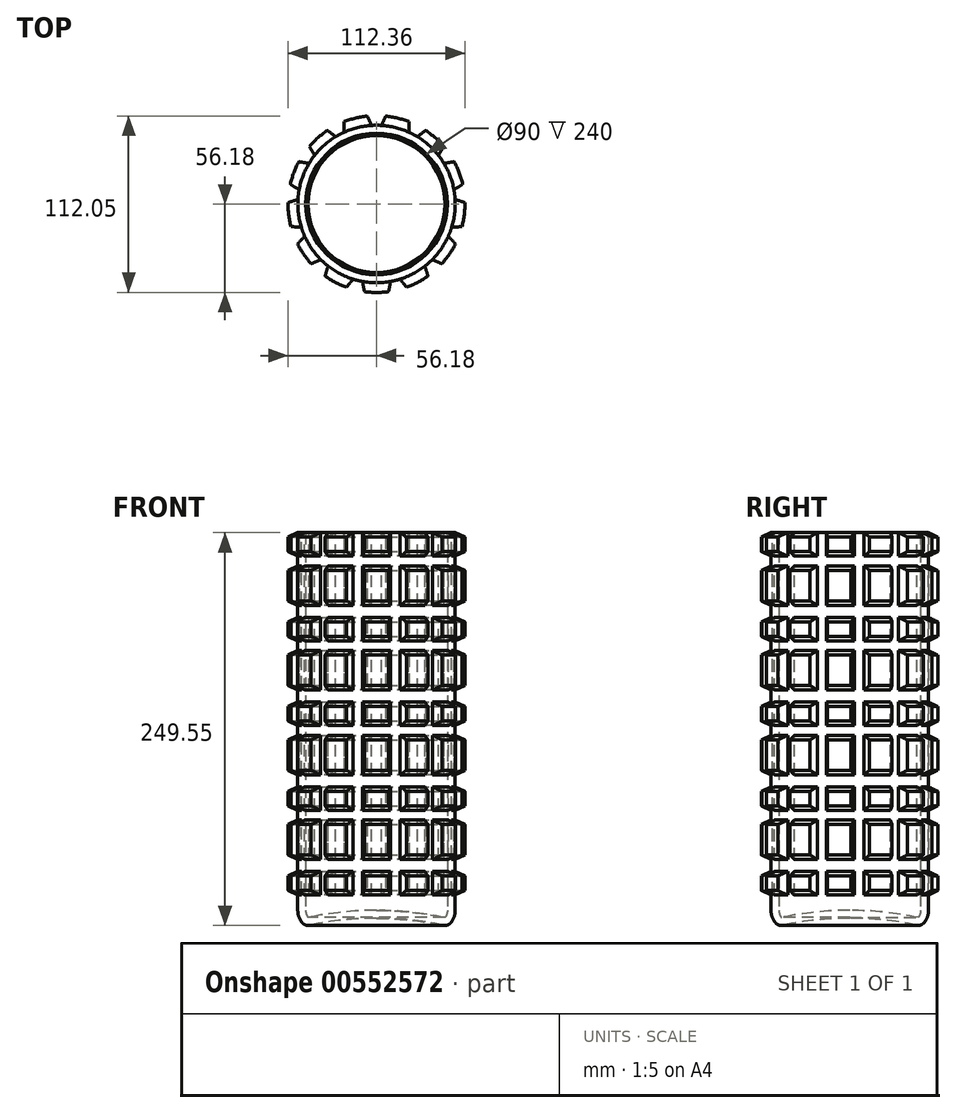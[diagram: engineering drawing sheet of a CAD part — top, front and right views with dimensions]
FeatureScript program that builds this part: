
annotation { "Feature Type Name" : "Feature", "Feature Type Description" : "" }
export const myFeature = defineFeature(function(context is Context, id is Id, definition is map)
    precondition{}
    {
        {
            var Q0;
            Q0=qCreatedBy(makeId("Front.planeOp"),FACE);
            var sketch = newSketch(context, id + "F0", { "sketchPlane" : qUnion([Q0])});
            skLineSegment(sketch, "E0", {"start": v(0, 125) * mm, "end": v(0, -125) * mm, "construction": true});
            skPoint(sketch, "E1", {"position": v(0, 0) * mm});
            skLineSegment(sketch, "E2", {"start": v(-50, 0) * mm, "end": v(50, 0) * mm, "construction": true});
            skLineSegment(sketch, "E3", {"start": v(-50, -115) * mm, "end": v(50, -115) * mm, "construction": true});
            skPoint(sketch, "E4", {"position": v(0, -115) * mm});
            skLineSegment(sketch, "E5", {"start": v(-45, -125) * mm, "end": v(45, -125) * mm, "construction": true});
            skPoint(sketch, "E6", {"position": v(0, -125) * mm});
            skLineSegment(sketch, "E7", {"start": v(0, 125) * mm, "end": v(50, 125) * mm, "construction": true});
            skLineSegment(sketch, "E8", {"start": v(50, 125) * mm, "end": v(0, 125) * mm});
            skLineSegment(sketch, "E9", {"start": v(0, -120) * mm, "end": v(45, -120) * mm, "construction": true});
            skLineSegment(sketch, "E10", {"start": v(50, -115) * mm, "end": v(50, 125) * mm, "construction": true});
            skArc(sketch, "E11", {"start": v(42.43, -124.44) * mm, "mid": v(21.33, -121.11) * mm, "end": v(0, -120) * mm});
            skArc(sketch, "E12", {"start": v(47.44, -122.58) * mm, "mid": v(49.34, -119) * mm, "end": v(50, -115) * mm});
            skPoint(sketch, "E13.visualSharp", {"position": v(45, -125) * mm});
            skArc(sketch, "E13.filletArc", {"start": v(42.43, -124.44) * mm, "mid": v(45.2, -124.23) * mm, "end": v(47.44, -122.58) * mm});
            skLineSegment(sketch, "E14", {"start": v(50, 125) * mm, "end": v(50, -115) * mm});
            skArc(sketch, "E15.0", {"start": v(43.46, -119.55) * mm, "mid": v(21.85, -116.14) * mm, "end": v(0, -115) * mm});
            skArc(sketch, "E15.1", {"start": v(43.46, -119.55) * mm, "mid": v(44.6, -117.4) * mm, "end": v(45, -115) * mm});
            skLineSegment(sketch, "E15.2", {"start": v(45, 125) * mm, "end": v(45, -115) * mm});
            skLineSegment(sketch, "E16", {"start": v(0, -120) * mm, "end": v(0, 125) * mm});
            skSolve(sketch);
        }
        {
            var Q0;
            {var subQ0=sQuery(id+"F0.wireOp",EDGE,"E11");Q0=makeQuery(id+"F0.imprint","IMPRINT",FACE,{"disambiguationData":[TD([[makeQuery(id+"F0.imprint","IMPRINT",EDGE,{"derivedFrom":subQ0}),-1.0]])]});}
            var Q1;
            Q1=sQuery(id+"F0.wireOp",EDGE,"E16");
            revolve(context, id + "F1", {"surfaceOperationType" : NewSurfaceOperationType.NEW, "entities" : qUnion([Q0]), "axis" : qUnion([Q1]), "revolveType" : RevolveType.FULL});
        }
        {
            var Q0;
            Q0=qCreatedBy(makeId("Front.planeOp"),FACE);
            var sketch = newSketch(context, id + "F2", { "sketchPlane" : qUnion([Q0])});
            skLineSegment(sketch, "E17.bottom", {"start": v(50, 125) * mm, "end": v(-50, 125) * mm, "construction": true});
            skLineSegment(sketch, "E17.top", {"start": v(50, -125) * mm, "end": v(-50, -125) * mm, "construction": true});
            skLineSegment(sketch, "E17.left", {"start": v(50, 125) * mm, "end": v(50, -125) * mm, "construction": true});
            skLineSegment(sketch, "E17.right", {"start": v(-50, 125) * mm, "end": v(-50, -125) * mm, "construction": true});
            skPoint(sketch, "E17.middle", {"position": v(0, 0) * mm});
            skLineSegment(sketch, "E18", {"start": v(50, 125) * mm, "end": v(56.18, 122.12) * mm});
            skLineSegment(sketch, "E19", {"start": v(56.18, 122.12) * mm, "end": v(56.18, 112.88) * mm});
            skLineSegment(sketch, "E20", {"start": v(56.18, 112.88) * mm, "end": v(50, 110) * mm});
            skLineSegment(sketch, "E21", {"start": v(0, 0) * mm, "end": v(0, -115) * mm, "construction": true});
            skLineSegment(sketch, "E22", {"start": v(0, -115) * mm, "end": v(50, -115) * mm, "construction": true});
            skPoint(sketch, "E23", {"position": v(50, 103.82) * mm});
            skLineSegment(sketch, "E24", {"start": v(50, 103.82) * mm, "end": v(56.18, 100.94) * mm});
            skLineSegment(sketch, "E25", {"start": v(56.18, 100.94) * mm, "end": v(56.18, 81.7) * mm});
            skLineSegment(sketch, "E26", {"start": v(56.18, 81.7) * mm, "end": v(50, 78.82) * mm});
            skLineSegment(sketch, "E27.0.1.0", {"start": v(50, 71.18) * mm, "end": v(56.18, 68.3) * mm});
            skLineSegment(sketch, "E27.0.1.1", {"start": v(56.18, 68.3) * mm, "end": v(56.18, 59.06) * mm});
            skLineSegment(sketch, "E27.0.1.2", {"start": v(56.18, 59.06) * mm, "end": v(50, 56.18) * mm});
            skLineSegment(sketch, "E27.0.1.3", {"start": v(50, 50) * mm, "end": v(56.18, 47.12) * mm});
            skLineSegment(sketch, "E27.0.1.4", {"start": v(56.18, 47.12) * mm, "end": v(56.18, 27.88) * mm});
            skLineSegment(sketch, "E27.0.1.5", {"start": v(56.18, 27.88) * mm, "end": v(50, 25) * mm});
            skLineSegment(sketch, "E27.0.2.0", {"start": v(50, 17.36) * mm, "end": v(56.18, 14.48) * mm});
            skLineSegment(sketch, "E27.0.2.1", {"start": v(56.18, 14.48) * mm, "end": v(56.18, 5.24) * mm});
            skLineSegment(sketch, "E27.0.2.2", {"start": v(56.18, 5.24) * mm, "end": v(50, 2.36) * mm});
            skLineSegment(sketch, "E27.0.2.3", {"start": v(50, -3.82) * mm, "end": v(56.18, -6.7) * mm});
            skLineSegment(sketch, "E27.0.2.4", {"start": v(56.18, -6.7) * mm, "end": v(56.18, -25.94) * mm});
            skLineSegment(sketch, "E27.0.2.5", {"start": v(56.18, -25.94) * mm, "end": v(50, -28.82) * mm});
            skLineSegment(sketch, "E27.direction1", {"start": v(50, 125) * mm, "end": v(75, 125) * mm, "construction": true});
            skLineSegment(sketch, "E27.direction2", {"start": v(50, 125) * mm, "end": v(50, 71.18) * mm, "construction": true});
            skLineSegment(sketch, "E28", {"start": v(50, -3.82) * mm, "end": v(50, -28.82) * mm});
            skLineSegment(sketch, "E29", {"start": v(50, 17.36) * mm, "end": v(50, 2.36) * mm});
            skLineSegment(sketch, "E30", {"start": v(50, 50) * mm, "end": v(50, 25) * mm});
            skLineSegment(sketch, "E31", {"start": v(50, 71.18) * mm, "end": v(50, 56.18) * mm});
            skLineSegment(sketch, "E32", {"start": v(50, 103.82) * mm, "end": v(50, 78.82) * mm});
            skLineSegment(sketch, "E33", {"start": v(50, 125) * mm, "end": v(50, 110) * mm});
            skLineSegment(sketch, "E34.0.0.3", {"start": v(50, -36.46) * mm, "end": v(56.18, -39.34) * mm});
            skLineSegment(sketch, "E34.3.0.3", {"start": v(56.18, -39.34) * mm, "end": v(56.18, -48.58) * mm});
            skLineSegment(sketch, "E34.6.0.3", {"start": v(56.18, -48.58) * mm, "end": v(50, -51.46) * mm});
            skLineSegment(sketch, "E34.9.0.3", {"start": v(50, -57.64) * mm, "end": v(56.18, -60.52) * mm});
            skLineSegment(sketch, "E34.12.0.3", {"start": v(56.18, -60.52) * mm, "end": v(56.18, -79.76) * mm});
            skLineSegment(sketch, "E34.15.0.3", {"start": v(56.18, -79.76) * mm, "end": v(50, -82.64) * mm});
            skLineSegment(sketch, "E35.0.0.4", {"start": v(50, -90.28) * mm, "end": v(56.18, -93.16) * mm});
            skLineSegment(sketch, "E35.3.0.4", {"start": v(56.18, -93.16) * mm, "end": v(56.18, -102.4) * mm});
            skLineSegment(sketch, "E35.6.0.4", {"start": v(56.18, -102.4) * mm, "end": v(50, -105.28) * mm});
            skLineSegment(sketch, "E36", {"start": v(50, -36.46) * mm, "end": v(50, -51.46) * mm});
            skLineSegment(sketch, "E37", {"start": v(50, -57.64) * mm, "end": v(50, -82.64) * mm});
            skLineSegment(sketch, "E38", {"start": v(50, -90.28) * mm, "end": v(50, -105.28) * mm});
            skSolve(sketch);
        }
        {
            var Q0;
            Q0=makeQuery(id+"F2.imprint","IMPRINT",FACE,{"disambiguationData":[TD([[makeQuery(id+"F2.imprint","IMPRINT",EDGE,{"derivedFrom":sQuery(id+"F2.wireOp",EDGE,"E18")}),-1.0]])]});
            var Q1;
            Q1=makeQuery(id+"F2.imprint","IMPRINT",FACE,{"disambiguationData":[TD([[makeQuery(id+"F2.imprint","IMPRINT",EDGE,{"derivedFrom":sQuery(id+"F2.wireOp",EDGE,"E24")}),-1.0]])]});
            var Q2;
            Q2=makeQuery(id+"F2.imprint","IMPRINT",FACE,{"disambiguationData":[TD([[makeQuery(id+"F2.imprint","IMPRINT",EDGE,{"derivedFrom":sQuery(id+"F2.wireOp",EDGE,"E27.0.1.0")}),-1.0]])]});
            var Q3;
            Q3=makeQuery(id+"F2.imprint","IMPRINT",FACE,{"disambiguationData":[TD([[makeQuery(id+"F2.imprint","IMPRINT",EDGE,{"derivedFrom":sQuery(id+"F2.wireOp",EDGE,"E27.0.1.3")}),-1.0]])]});
            var Q4;
            Q4=makeQuery(id+"F2.imprint","IMPRINT",FACE,{"disambiguationData":[TD([[makeQuery(id+"F2.imprint","IMPRINT",EDGE,{"derivedFrom":sQuery(id+"F2.wireOp",EDGE,"E27.0.2.0")}),-1.0]])]});
            var Q5;
            Q5=makeQuery(id+"F2.imprint","IMPRINT",FACE,{"disambiguationData":[TD([[makeQuery(id+"F2.imprint","IMPRINT",EDGE,{"derivedFrom":sQuery(id+"F2.wireOp",EDGE,"E27.0.2.3")}),-1.0]])]});
            var Q6;
            Q6=makeQuery(id+"F2.imprint","IMPRINT",FACE,{"disambiguationData":[TD([[makeQuery(id+"F2.imprint","IMPRINT",EDGE,{"derivedFrom":sQuery(id+"F2.wireOp",EDGE,"yBdnIs5V-2HzW-Vo2F-MoPb-cdSNorzKz5Gy")}),-1.0]])]});
            var Q7;
            Q7=makeQuery(id+"F2.imprint","IMPRINT",FACE,{"disambiguationData":[TD([[makeQuery(id+"F2.imprint","IMPRINT",EDGE,{"derivedFrom":sQuery(id+"F2.wireOp",EDGE,"E34.0.0.3")}),-1.0]])]});
            var Q8;
            Q8=makeQuery(id+"F2.imprint","IMPRINT",FACE,{"disambiguationData":[TD([[makeQuery(id+"F2.imprint","IMPRINT",EDGE,{"derivedFrom":sQuery(id+"F2.wireOp",EDGE,"E34.9.0.3")}),-1.0]])]});
            var Q9;
            Q9=makeQuery(id+"F2.imprint","IMPRINT",FACE,{"disambiguationData":[TD([[makeQuery(id+"F2.imprint","IMPRINT",EDGE,{"derivedFrom":sQuery(id+"F2.wireOp",EDGE,"E35.0.0.4")}),-1.0]])]});
            var Q10;
            Q10=sQuery(id+"F0.wireOp",EDGE,"E16");
            revolve(context, id + "F3", {"operationType" : NewBodyOperationType.ADD, "surfaceOperationType" : NewSurfaceOperationType.NEW, "entities" : qUnion([Q0, Q1, Q2, Q3, Q4, Q5, Q6, Q7, Q8, Q9]), "axis" : qUnion([Q10]), "revolveType" : RevolveType.FULL});
        }
        {
            var Q0;
            Q0=qCreatedBy(makeId("Top.planeOp"),FACE);
            cPlane(context, id + "F4", {"entities" : qUnion([Q0]), "cplaneType" : CPlaneType.OFFSET, "offset" : 140 * mm, "width" : 150 * mm, "height" : 150 * mm});
        }
        {
            var Q0;
            Q0=qCreatedBy(id+"F4.planeOp",FACE);
            var sketch = newSketch(context, id + "F5", { "sketchPlane" : qUnion([Q0])});
            skCircle(sketch, "E39", {"center": v(0, 0) * mm, "radius": 50 * mm, "construction": true});
            skLineSegment(sketch, "E40", {"start": v(0, 0) * mm, "end": v(0, 50) * mm, "construction": true});
            skPoint(sketch, "E41", {"position": v(0, 50) * mm});
            skLineSegment(sketch, "E42", {"start": v(0, 50) * mm, "end": v(0, 54.92) * mm, "construction": true});
            skArc(sketch, "E43", {"start": v(3.1, 49.9) * mm, "mid": v(0, 50) * mm, "end": v(-3.1, 49.9) * mm});
            skLineSegment(sketch, "E44", {"start": v(3.1, 49.9) * mm, "end": v(8.17, 60.8) * mm});
            skLineSegment(sketch, "E45", {"start": v(-8.17, 60.8) * mm, "end": v(-3.1, 49.9) * mm});
            skArc(sketch, "E46", {"start": v(8.17, 60.8) * mm, "mid": v(0, 61.48) * mm, "end": v(-8.17, 60.8) * mm});
            skLineSegment(sketch, "E47.1.0", {"start": v(-35.5, 50.04) * mm, "end": v(-25.93, 42.75) * mm});
            skArc(sketch, "E47.1.1", {"start": v(-21.02, 57.64) * mm, "mid": v(-28.57, 54.43) * mm, "end": v(-35.5, 50.04) * mm});
            skLineSegment(sketch, "E47.1.2", {"start": v(-20.46, 45.62) * mm, "end": v(-21.02, 57.64) * mm});
            skArc(sketch, "E47.1.3", {"start": v(-20.46, 45.62) * mm, "mid": v(-23.24, 44.27) * mm, "end": v(-25.93, 42.75) * mm});
            skLineSegment(sketch, "E47.2.0", {"start": v(-54.68, 27.81) * mm, "end": v(-42.83, 25.8) * mm});
            skArc(sketch, "E47.2.1", {"start": v(-45.4, 41.27) * mm, "mid": v(-50.6, 34.92) * mm, "end": v(-54.68, 27.81) * mm});
            skLineSegment(sketch, "E47.2.2", {"start": v(-39.32, 30.9) * mm, "end": v(-45.4, 41.27) * mm});
            skArc(sketch, "E47.2.3", {"start": v(-39.32, 30.9) * mm, "mid": v(-41.15, 28.4) * mm, "end": v(-42.83, 25.8) * mm});
            skLineSegment(sketch, "E47.3.0", {"start": v(-61.35, -0.78) * mm, "end": v(-49.91, 2.95) * mm});
            skArc(sketch, "E47.3.1", {"start": v(-59.38, 15.44) * mm, "mid": v(-61.03, 7.41) * mm, "end": v(-61.35, -0.78) * mm});
            skLineSegment(sketch, "E47.3.2", {"start": v(-49.17, 9.08) * mm, "end": v(-59.38, 15.44) * mm});
            skArc(sketch, "E47.3.3", {"start": v(-49.17, 9.08) * mm, "mid": v(-49.64, 6.03) * mm, "end": v(-49.91, 2.95) * mm});
            skLineSegment(sketch, "E47.4.0", {"start": v(-53.95, -29.2) * mm, "end": v(-45.57, -20.59) * mm});
            skArc(sketch, "E47.4.1", {"start": v(-59.75, -13.92) * mm, "mid": v(-57.48, -21.8) * mm, "end": v(-53.95, -29.2) * mm});
            skLineSegment(sketch, "E47.4.2", {"start": v(-47.76, -14.8) * mm, "end": v(-59.75, -13.92) * mm});
            skArc(sketch, "E47.4.3", {"start": v(-47.76, -14.8) * mm, "mid": v(-46.75, -17.73) * mm, "end": v(-45.57, -20.59) * mm});
            skLineSegment(sketch, "E47.5.0", {"start": v(-34.2, -50.93) * mm, "end": v(-30.78, -39.4) * mm});
            skArc(sketch, "E47.5.1", {"start": v(-46.44, -40.1) * mm, "mid": v(-40.77, -46.02) * mm, "end": v(-34.2, -50.93) * mm});
            skLineSegment(sketch, "E47.5.2", {"start": v(-35.4, -35.3) * mm, "end": v(-46.44, -40.1) * mm});
            skArc(sketch, "E47.5.3", {"start": v(-35.4, -35.3) * mm, "mid": v(-33.16, -37.43) * mm, "end": v(-30.78, -39.4) * mm});
            skLineSegment(sketch, "E47.6.0", {"start": v(-6.62, -61) * mm, "end": v(-8.94, -49.2) * mm});
            skArc(sketch, "E47.6.1", {"start": v(-22.49, -57.08) * mm, "mid": v(-14.71, -59.7) * mm, "end": v(-6.62, -61) * mm});
            skLineSegment(sketch, "E47.6.2", {"start": v(-14.94, -47.71) * mm, "end": v(-22.49, -57.08) * mm});
            skArc(sketch, "E47.6.3", {"start": v(-14.94, -47.71) * mm, "mid": v(-11.97, -48.55) * mm, "end": v(-8.94, -49.2) * mm});
            skLineSegment(sketch, "E47.7.0", {"start": v(22.49, -57.08) * mm, "end": v(14.94, -47.71) * mm});
            skArc(sketch, "E47.7.1", {"start": v(6.62, -61) * mm, "mid": v(14.71, -59.7) * mm, "end": v(22.49, -57.08) * mm});
            skLineSegment(sketch, "E47.7.2", {"start": v(8.94, -49.2) * mm, "end": v(6.62, -61) * mm});
            skArc(sketch, "E47.7.3", {"start": v(8.94, -49.2) * mm, "mid": v(11.97, -48.55) * mm, "end": v(14.94, -47.71) * mm});
            skLineSegment(sketch, "E47.8.0", {"start": v(46.44, -40.1) * mm, "end": v(35.4, -35.3) * mm});
            skArc(sketch, "E47.8.1", {"start": v(34.2, -50.93) * mm, "mid": v(40.77, -46.02) * mm, "end": v(46.44, -40.1) * mm});
            skLineSegment(sketch, "E47.8.2", {"start": v(30.78, -39.4) * mm, "end": v(34.2, -50.93) * mm});
            skArc(sketch, "E47.8.3", {"start": v(30.78, -39.4) * mm, "mid": v(33.16, -37.43) * mm, "end": v(35.4, -35.3) * mm});
            skLineSegment(sketch, "E47.9.0", {"start": v(59.75, -13.92) * mm, "end": v(47.76, -14.8) * mm});
            skArc(sketch, "E47.9.1", {"start": v(53.95, -29.2) * mm, "mid": v(57.48, -21.8) * mm, "end": v(59.75, -13.92) * mm});
            skLineSegment(sketch, "E47.9.2", {"start": v(45.57, -20.59) * mm, "end": v(53.95, -29.2) * mm});
            skArc(sketch, "E47.9.3", {"start": v(45.57, -20.59) * mm, "mid": v(46.75, -17.73) * mm, "end": v(47.76, -14.8) * mm});
            skLineSegment(sketch, "E47.10.0", {"start": v(59.38, 15.44) * mm, "end": v(49.17, 9.08) * mm});
            skArc(sketch, "E47.10.1", {"start": v(61.35, -0.78) * mm, "mid": v(61.03, 7.41) * mm, "end": v(59.38, 15.44) * mm});
            skLineSegment(sketch, "E47.10.2", {"start": v(49.91, 2.95) * mm, "end": v(61.35, -0.78) * mm});
            skArc(sketch, "E47.10.3", {"start": v(49.91, 2.95) * mm, "mid": v(49.64, 6.03) * mm, "end": v(49.17, 9.08) * mm});
            skLineSegment(sketch, "E47.11.0", {"start": v(45.4, 41.27) * mm, "end": v(39.32, 30.9) * mm});
            skArc(sketch, "E47.11.1", {"start": v(54.68, 27.81) * mm, "mid": v(50.6, 34.92) * mm, "end": v(45.4, 41.27) * mm});
            skLineSegment(sketch, "E47.11.2", {"start": v(42.83, 25.8) * mm, "end": v(54.68, 27.81) * mm});
            skArc(sketch, "E47.11.3", {"start": v(42.83, 25.8) * mm, "mid": v(41.15, 28.4) * mm, "end": v(39.32, 30.9) * mm});
            skLineSegment(sketch, "E47.12.0", {"start": v(21.02, 57.64) * mm, "end": v(20.46, 45.62) * mm});
            skArc(sketch, "E47.12.1", {"start": v(35.5, 50.04) * mm, "mid": v(28.57, 54.43) * mm, "end": v(21.02, 57.64) * mm});
            skLineSegment(sketch, "E47.12.2", {"start": v(25.93, 42.75) * mm, "end": v(35.5, 50.04) * mm});
            skArc(sketch, "E47.12.3", {"start": v(25.93, 42.75) * mm, "mid": v(23.24, 44.27) * mm, "end": v(20.46, 45.62) * mm});
            skSolve(sketch);
        }
        {
            var Q0;
            Q0=makeQuery(id+"F5.imprint","IMPRINT",FACE,{"disambiguationData":[TD([[makeQuery(id+"F5.imprint","IMPRINT",EDGE,{"derivedFrom":sQuery(id+"F5.wireOp",EDGE,"E47.1.0")}),1.0]])]});
            var Q1;
            Q1=makeQuery(id+"F5.imprint","IMPRINT",FACE,{"disambiguationData":[TD([[makeQuery(id+"F5.imprint","IMPRINT",EDGE,{"derivedFrom":sQuery(id+"F5.wireOp",EDGE,"E43")}),-1.0]])]});
            var Q2;
            Q2=makeQuery(id+"F5.imprint","IMPRINT",FACE,{"disambiguationData":[TD([[makeQuery(id+"F5.imprint","IMPRINT",EDGE,{"derivedFrom":sQuery(id+"F5.wireOp",EDGE,"E47.12.0")}),1.0]])]});
            var Q3;
            Q3=makeQuery(id+"F5.imprint","IMPRINT",FACE,{"disambiguationData":[TD([[makeQuery(id+"F5.imprint","IMPRINT",EDGE,{"derivedFrom":sQuery(id+"F5.wireOp",EDGE,"E47.2.0")}),1.0]])]});
            var Q4;
            Q4=makeQuery(id+"F5.imprint","IMPRINT",FACE,{"disambiguationData":[TD([[makeQuery(id+"F5.imprint","IMPRINT",EDGE,{"derivedFrom":sQuery(id+"F5.wireOp",EDGE,"E47.3.0")}),1.0]])]});
            var Q5;
            Q5=makeQuery(id+"F5.imprint","IMPRINT",FACE,{"disambiguationData":[TD([[makeQuery(id+"F5.imprint","IMPRINT",EDGE,{"derivedFrom":sQuery(id+"F5.wireOp",EDGE,"E47.4.0")}),1.0]])]});
            var Q6;
            Q6=makeQuery(id+"F5.imprint","IMPRINT",FACE,{"disambiguationData":[TD([[makeQuery(id+"F5.imprint","IMPRINT",EDGE,{"derivedFrom":sQuery(id+"F5.wireOp",EDGE,"E47.5.0")}),1.0]])]});
            var Q7;
            Q7=makeQuery(id+"F5.imprint","IMPRINT",FACE,{"disambiguationData":[TD([[makeQuery(id+"F5.imprint","IMPRINT",EDGE,{"derivedFrom":sQuery(id+"F5.wireOp",EDGE,"E47.6.0")}),1.0]])]});
            var Q8;
            Q8=makeQuery(id+"F5.imprint","IMPRINT",FACE,{"disambiguationData":[TD([[makeQuery(id+"F5.imprint","IMPRINT",EDGE,{"derivedFrom":sQuery(id+"F5.wireOp",EDGE,"E47.7.0")}),1.0]])]});
            var Q9;
            Q9=makeQuery(id+"F5.imprint","IMPRINT",FACE,{"disambiguationData":[TD([[makeQuery(id+"F5.imprint","IMPRINT",EDGE,{"derivedFrom":sQuery(id+"F5.wireOp",EDGE,"E47.8.0")}),1.0]])]});
            var Q10;
            Q10=makeQuery(id+"F5.imprint","IMPRINT",FACE,{"disambiguationData":[TD([[makeQuery(id+"F5.imprint","IMPRINT",EDGE,{"derivedFrom":sQuery(id+"F5.wireOp",EDGE,"E47.9.0")}),1.0]])]});
            var Q11;
            Q11=makeQuery(id+"F5.imprint","IMPRINT",FACE,{"disambiguationData":[TD([[makeQuery(id+"F5.imprint","IMPRINT",EDGE,{"derivedFrom":sQuery(id+"F5.wireOp",EDGE,"E47.10.0")}),1.0]])]});
            var Q12;
            Q12=makeQuery(id+"F5.imprint","IMPRINT",FACE,{"disambiguationData":[TD([[makeQuery(id+"F5.imprint","IMPRINT",EDGE,{"derivedFrom":sQuery(id+"F5.wireOp",EDGE,"E47.11.0")}),1.0]])]});
            extrude(context, id + "F6", {"entities" : qUnion([Q0, Q1, Q2, Q3, Q4, Q5, Q6, Q7, Q8, Q9, Q10, Q11, Q12]), "operationType" : NewBodyOperationType.REMOVE, "endBound" : BoundingType.THROUGH_ALL, "oppositeDirection" : true, "depth" : 25 * mm, "offsetDistance" : 25 * mm});
        }
    });
